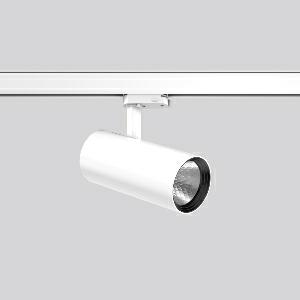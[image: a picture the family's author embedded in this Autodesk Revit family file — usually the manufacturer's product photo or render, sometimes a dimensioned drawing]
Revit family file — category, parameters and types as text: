
# Revit family: deecos_s_mini_742196_002_2_76_93c0
name_source: partatom
category: Lighting Fixtures
units: mm (PartAtom-declared; Revit-internal decimal feet)

## family parameters
Cut with Voids When Loaded = No
Host = Face
Light Source = No
Part Type = Normal
Room Calculation Point = No
Round Connector Dimension = Use Diameter
Shared = No

## types (1)
- DEECOS S mini (1 x LED Modul 927, 2300 lm, 2700)
    Apparent Load = 20 VA
    Approval mark = CE
    CIE Flux Codes = 99 100 100 100 100
    Color Rendering = 92
    Color Temperature = 2700
    Default Elevation = 1800 mm
    Description = Series: DEECOS S mini
LED surface-mounted projector in modern design with no visible cooling ribs. Housing: die-cast aluminium, powder-coated. Rotation range: 356°. Swivel range: 90°. Black plastic ring and recessed LED to prevent glare from the side. Optical assembly with reflector made of MIRO-Silver with 98% total light reflection for outstanding efficiency - can be changed without tools. Best colour rendering index Ra>90. With adapter for RZB 3-circuit DALI tracks. Suitable for Track on ceiling, Wall track. High quality converter without flickering and stroboscopic effect. The following accessories can be mounted without use of tools: interchangeable lenses, decorative glasses, honeycomb louvre, clear and frosted diffusers, white interchangeable plastic ring. 
Colour: traffic white, matt (RAL 9016)
Diameter: 87 mm
Height: 214 mm
Lamp: LED
Socket: without socket
Colour temperature: 2700K
Colour rendering index (CRI): 92
System power: 20 W
Rated luminous flux: 2300 lm
Luminous efficiency: 115 lm/W
Control gear: Converter, dimmable, DALI
Protection class: I
Type of protection: IP 20
    Height = 214 mm
    Lamp = 1 x LED Modul 927
    Lamp Light Flux = 2300 lm
    Lamp count = 1
    Length = 87 mm
    Lifetime = 50000 h
    Luminous efficacy = 115 lm/W
    Manufacturer = RZB
    ModVariant = No
    Model = 742196.002.2.76
    Mounting Place = Ceiling
    Mounting Type = Rail mounted
    Number of Poles = 1
    OnlyDefault = Yes
    Power Factor = 1
    Product Name = DEECOS S mini
    Product group = Track mounted projectors
    ProductGroupID = 301
    Protection Class = Protection class I
    Protection Degree = IP 20
    RLX_Detail_Level = 1
    RLX_Emergency_Light_Flux = 0 lm
    RLX_Emergency_Type = 0
    RLX_Emergency_Type_DB = No
    RlxData = <blob elided: 35013 chars, md5=ff916f10>
    Socket = socket
    Standby Power = 0 W
    System Light Flux = 2300 lm
    System Power = 20 W
    Type Comments = Product without accessories
    Type Image = 741926.002.jpg
    URL = http://relux.com
    VarID = ---
    Voltage = 230 V
    Voltage Range = 220-240 V
    Weight = 0.00 kg
    Width = 0 mm  [stored 0 ft]

note: [stored X ft] marks values corroborated as IEEE doubles in the binary element streams (Revit-internal decimal feet)

## geometry (parser evidence)
native form markers: Blend x4, Sweep x12
no freeform markers — native parametric forms only
